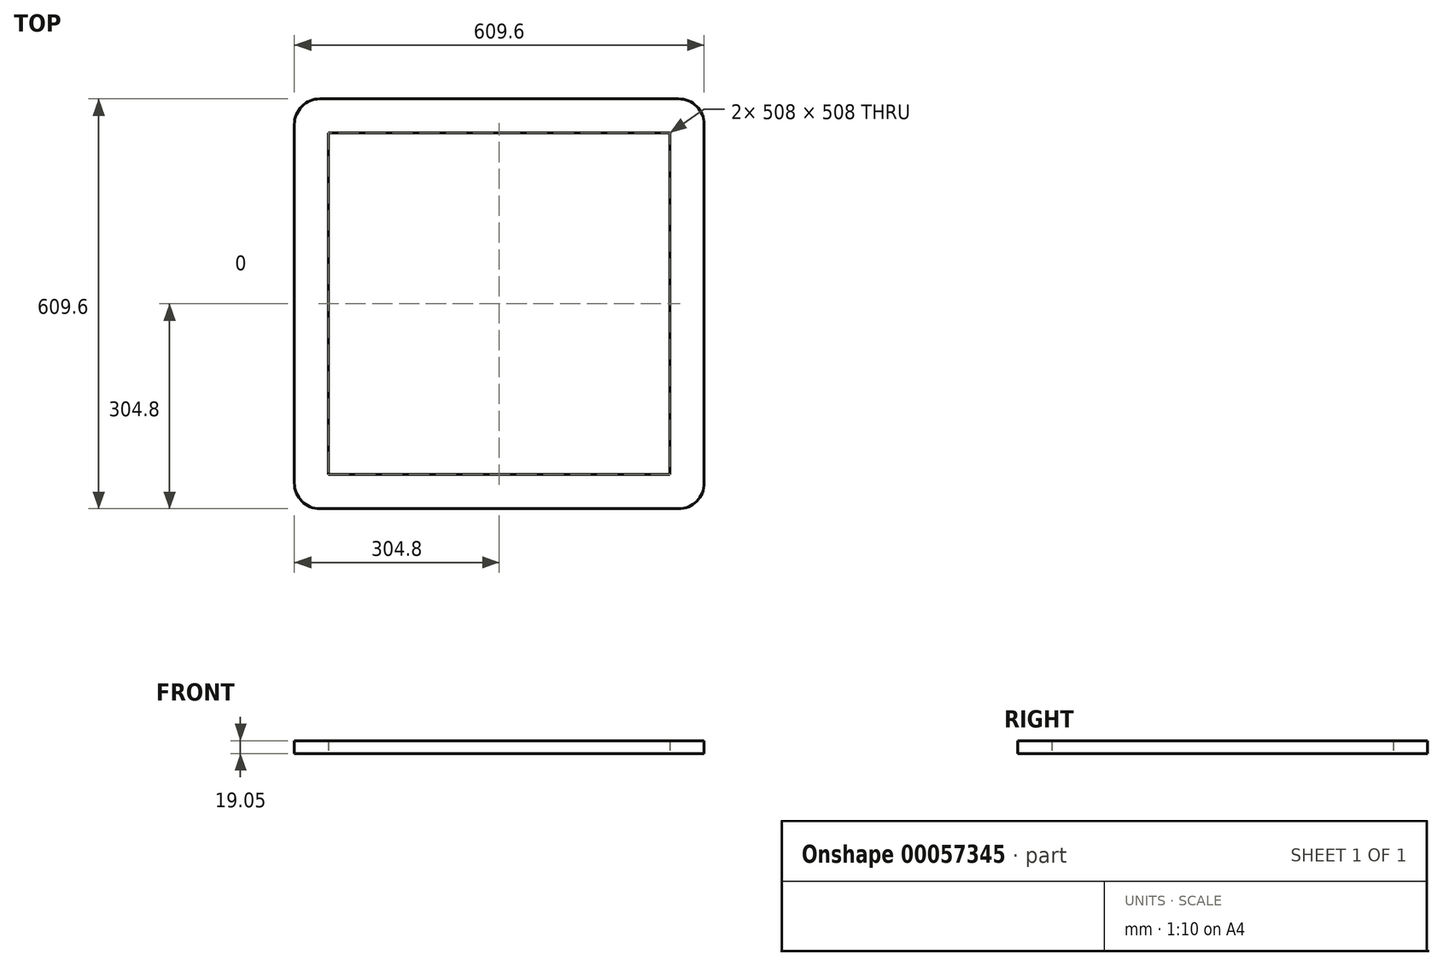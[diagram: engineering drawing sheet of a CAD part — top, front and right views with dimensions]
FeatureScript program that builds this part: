
annotation { "Feature Type Name" : "Feature", "Feature Type Description" : "" }
export const myFeature = defineFeature(function(context is Context, id is Id, definition is map)
    precondition{}
    {
        {
            var Q0;
            Q0=qCreatedBy(makeId("Top.planeOp"),FACE);
            var sketch = newSketch(context, id + "F0", { "sketchPlane" : qUnion([Q0])});
            skLineSegment(sketch, "E0.rect.bottom", {"start": v(304.8, -304.8) * mm, "end": v(-304.8, -304.8) * mm});
            skLineSegment(sketch, "E0.rect.top", {"start": v(304.8, 304.8) * mm, "end": v(-304.8, 304.8) * mm});
            skLineSegment(sketch, "E0.rect.left", {"start": v(304.8, -304.8) * mm, "end": v(304.8, 304.8) * mm});
            skLineSegment(sketch, "E0.rect.right", {"start": v(-304.8, -304.8) * mm, "end": v(-304.8, 304.8) * mm});
            skPoint(sketch, "E0.rect.middle", {"position": v(0, 0) * mm});
            skLineSegment(sketch, "E1.rect.bottom", {"start": v(-254, 254) * mm, "end": v(254, 254) * mm});
            skLineSegment(sketch, "E1.rect.top", {"start": v(-254, -254) * mm, "end": v(254, -254) * mm});
            skLineSegment(sketch, "E1.rect.left", {"start": v(-254, 254) * mm, "end": v(-254, -254) * mm});
            skLineSegment(sketch, "E1.rect.right", {"start": v(254, 254) * mm, "end": v(254, -254) * mm});
            skSolve(sketch);
        }
        {
            var Q0;
            Q0=makeQuery(id+"F0.imprint","IMPRINT",FACE,{"disambiguationData":[TD([[makeQuery(id+"F0.imprint","IMPRINT",EDGE,{"derivedFrom":sQuery(id+"F0.wireOp",EDGE,"E0.rect.bottom")}),-1.0]])]});
            extrude(context, id + "F1", {"entities" : qUnion([Q0]), "depth" : 19.05 * mm});
        }
        {
            var Q0;
            Q0=makeQuery(id+"F1.opExtrude","SWEPT_EDGE",EDGE,{"disambiguationData":[OSD([sQuery(id+"F0.wireOp",EDGE,"E0.rect.bottom"),sQuery(id+"F0.wireOp",EDGE,"E0.rect.right")])]});
            var Q1;
            Q1=makeQuery(id+"F1.opExtrude","SWEPT_EDGE",EDGE,{"disambiguationData":[OSD([sQuery(id+"F0.wireOp",EDGE,"E0.rect.bottom"),sQuery(id+"F0.wireOp",EDGE,"E0.rect.left")])]});
            var Q2;
            Q2=makeQuery(id+"F1.opExtrude","SWEPT_EDGE",EDGE,{"disambiguationData":[OSD([sQuery(id+"F0.wireOp",EDGE,"E0.rect.top"),sQuery(id+"F0.wireOp",EDGE,"E0.rect.left")])]});
            var Q3;
            Q3=makeQuery(id+"F1.opExtrude","SWEPT_EDGE",EDGE,{"disambiguationData":[OSD([sQuery(id+"F0.wireOp",EDGE,"E0.rect.top"),sQuery(id+"F0.wireOp",EDGE,"E0.rect.right")])]});
            fillet(context, id + "F2", {"entities" : qUnion([Q0, Q1, Q2, Q3]), "radius" : 38.1 * mm, "tangentPropagation" : true, "allowEdgeOverflow" : false});
        }
    });
